# Revit family: Bidet-Wall_Mount-DXV-Modulus-D25010001.415
name_source: partatom
category: Plumbing Fixtures
units: mm (PartAtom-declared; Revit-internal decimal feet)

## family parameters
Cut with Voids When Loaded = No
Host = Face
OmniClass Number = 23.45.05.14.27
OmniClass Title = Bidets
Part Type = Normal
Room Calculation Point = No
Round Connector Dimension = Use Diameter
Shared = Yes

## types (1)
- D25010001.415
    ASME A112.19.2/CSA B45.1 = Yes
    Assembly Code = D2010910
    CW Connection = Yes
    CWFU = 1.5
    Cold Water Connection Diameter = 3/8"
    Cold Water Connection Radius = 3/16"
    Cold Water Connection Width = 3"
    D25010001.415 Wall Hung Bidet = Yes
    D29050044.000 Wall Hung Bidet Carrier = Yes
    D35120012.XXX Bidet Faucet = Yes
    Default Elevation = 14 5/16"
    Description = DXV Modulus Wall-Mounted Bidet
    Finish = Vitreous China-DXV-415-Canvas White
    HW Connection = Yes
    HWFU = 1.5
    Height = 11 13/16"
    Hot Water Connection Diameter = 3/8"
    Hot Water Connection Height = 9"
    Hot Water Connection Width = 3"
    Installation Instruction Link = https://dxv01.blob.core.windows.net
    Installation Type = Wall Mounted
    Length = 22"
    Manufacturer = DXV
    Material = Vitreous China-DXV-415-Canvas White
    Model = D25010001.415
    Mounting Height = 17"
    Outlet Connection Height = 0"
    Outlet Height Input = 3 15/16"
    Price = Prices may vary. Please consult Manufacturer Representative for most up-to-date price list.
    Product Documentation Link = https://dxv01.blob.core.windows.net
    Product Page URL = https://www.dxv.com
    Revised Date = 03/07/2022
    URL = https://www.dxv.com
    Vent Connection = No
    WFU = 2
    Warranty Documentation Link = https://dxv01.blob.core.windows.net
    Waste Connection = Yes
    Waste Connection Diameter = 1 1/4"
    Waste Connection Height = 3 15/16"
    Width = 14 1/8"

## geometry (parser evidence)
native form markers: Sweep x3
no freeform markers — native parametric forms only
